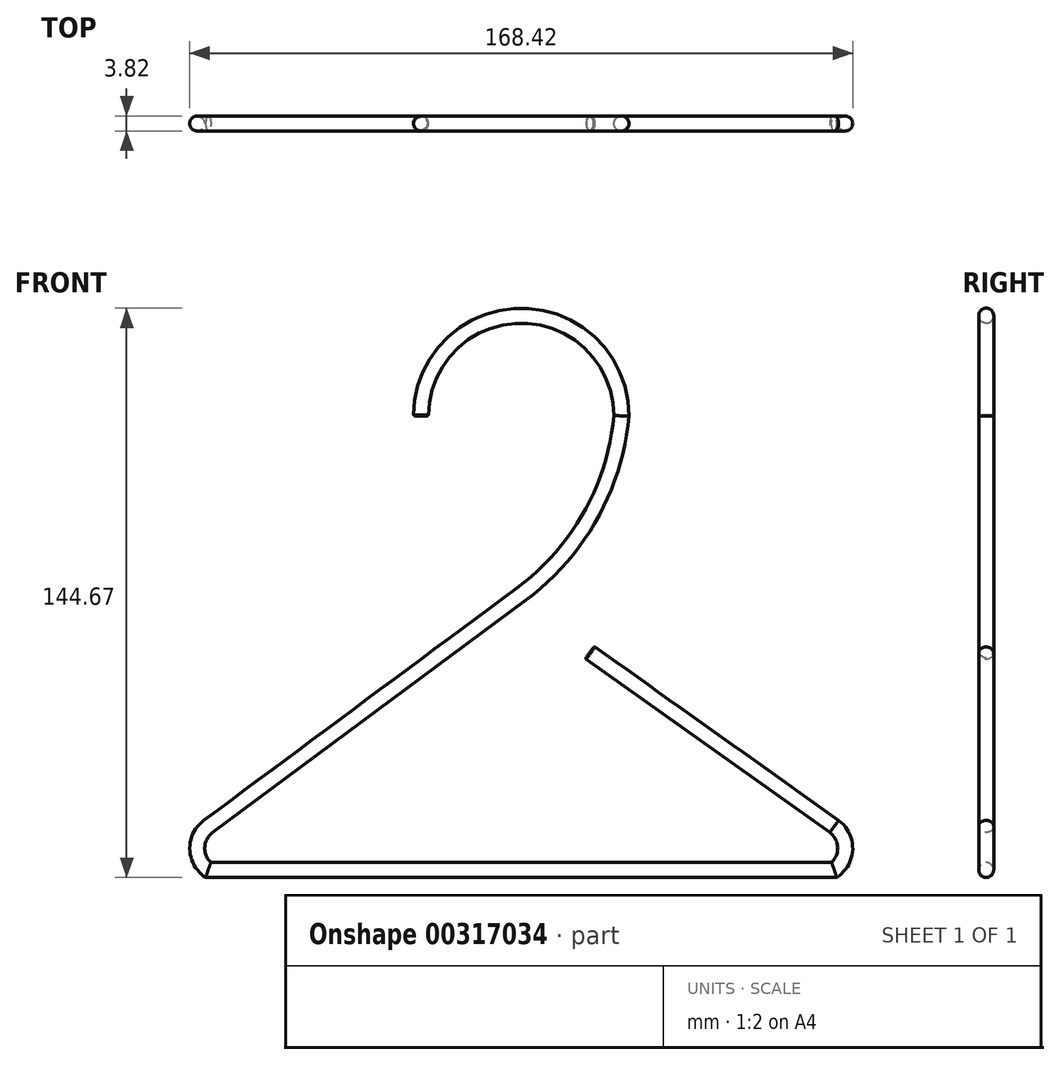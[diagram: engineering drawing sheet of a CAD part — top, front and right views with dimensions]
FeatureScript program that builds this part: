
annotation { "Feature Type Name" : "Feature", "Feature Type Description" : "" }
export const myFeature = defineFeature(function(context is Context, id is Id, definition is map)
    precondition{}
    {
        {
            var Q0;
            Q0=qCreatedBy(makeId("Front.planeOp"),FACE);
            var sketch = newSketch(context, id + "F0", { "sketchPlane" : qUnion([Q0])});
            skArc(sketch, "E0", {"start": v(25.4, 0) * mm, "mid": v(0, 25.4) * mm, "end": v(-25.4, 0) * mm});
            skArc(sketch, "E1", {"start": v(0, -45.23) * mm, "mid": v(17.53, -25.33) * mm, "end": v(25.4, 0) * mm});
            skLineSegment(sketch, "E2", {"start": v(0, -45.23) * mm, "end": v(-79.55, -104.26) * mm});
            skArc(sketch, "E3", {"start": v(-79.55, -104.26) * mm, "mid": v(-82.37, -109.86) * mm, "end": v(-79.55, -115.46) * mm});
            skLineSegment(sketch, "E4", {"start": v(0, -45.23) * mm, "end": v(0, -60.28) * mm, "construction": true});
            skArc(sketch, "E5", {"start": v(79.55, -115.46) * mm, "mid": v(82.37, -109.86) * mm, "end": v(79.55, -104.26) * mm});
            skLineSegment(sketch, "E6", {"start": v(-79.55, -115.46) * mm, "end": v(79.55, -115.46) * mm});
            skLineSegment(sketch, "E7", {"start": v(79.55, -104.26) * mm, "end": v(17.47, -60.08) * mm});
            skSolve(sketch);
        }
        {
            var Q0;
            Q0=qCreatedBy(makeId("Top.planeOp"),FACE);
            var sketch = newSketch(context, id + "F1", { "sketchPlane" : qUnion([Q0])});
            skCircle(sketch, "E8", {"center": v(-25.46, 0) * mm, "radius": 1.9 * mm});
            skSolve(sketch);
        }
        {
            var Q0;
            Q0 = qSketchRegion(id + "F1", true);
            var Q1;
            Q1 = qConstructionFilter(qBodyType(qCreatedBy(id + "F0" ,EDGE), BodyType.WIRE), ConstructionObject.NO);
            sweep(context, id + "F2", {"profiles" : qUnion([Q0]), "path" : qUnion([Q1])});
        }
        {
            var Q0;
            Q0=makeQuery(id+"F2.opSweep","CAP_EDGE",EDGE,{"disambiguationData":[OSD([sQuery(id+"F0.wireOp",VERTEX,"E0.end"),sQuery(id+"F1.wireOp",EDGE,"E8")])],"isStart":true});
            chamfer(context, id + "F3", {"entities" : qUnion([Q0]), "width" : 0.25 * mm, "tangentPropagation" : true});
        }
        {
            var Q0;
            Q0=makeQuery(id+"F2.opSweep","CAP_EDGE",EDGE,{"disambiguationData":[OSD([sQuery(id+"F0.wireOp",VERTEX,"E7.end"),sQuery(id+"F1.wireOp",EDGE,"E8")])],"isStart":false});
            chamfer(context, id + "F4", {"entities" : qUnion([Q0]), "width" : 0.25 * mm, "tangentPropagation" : true});
        }
    });
